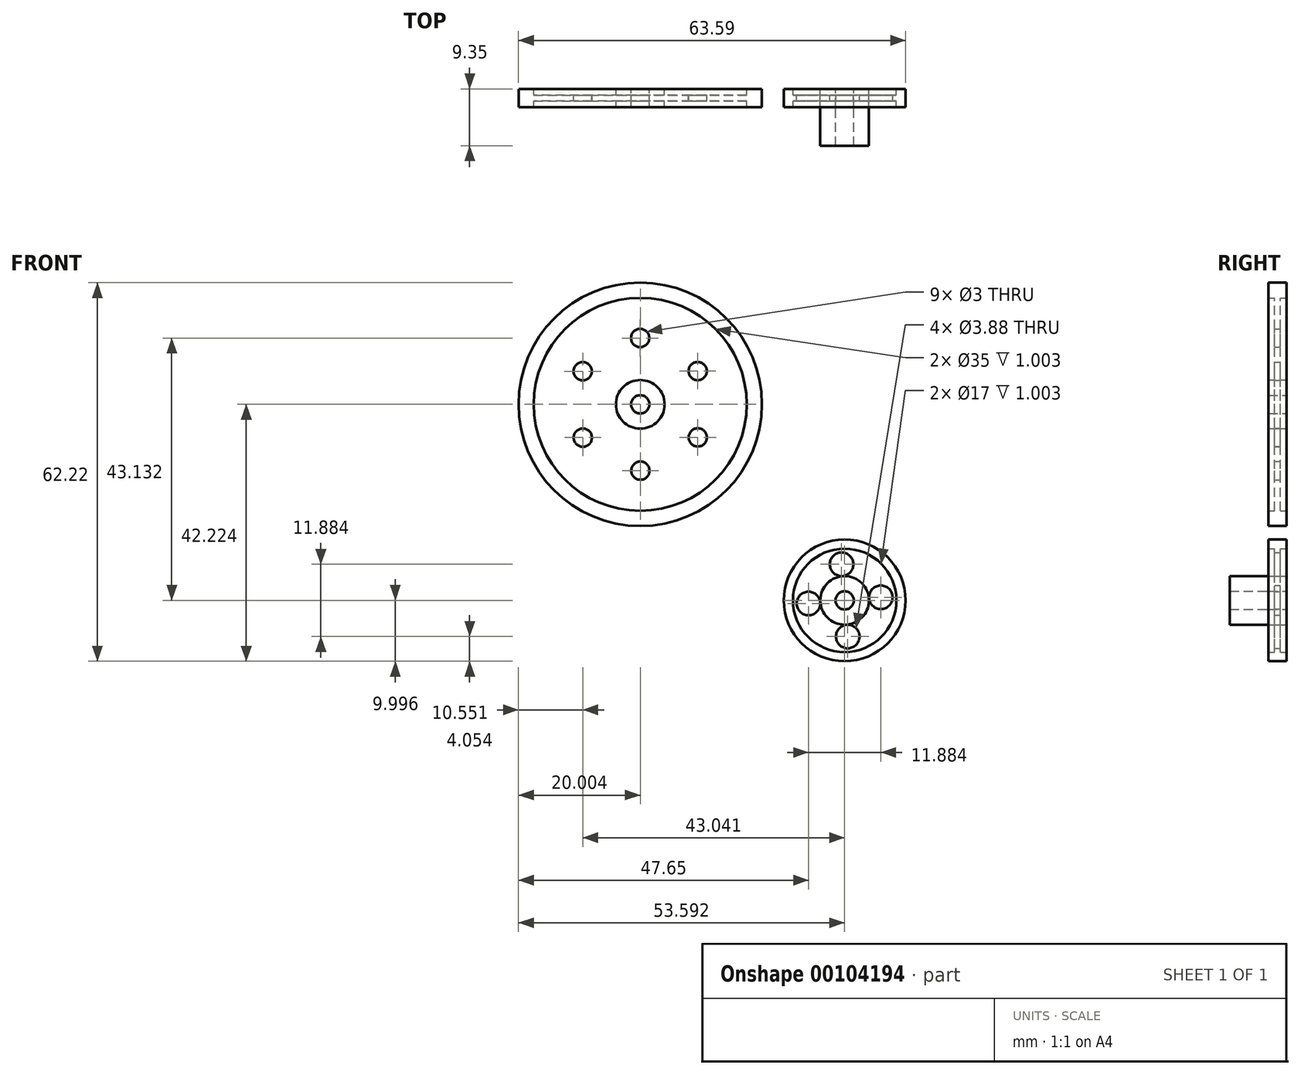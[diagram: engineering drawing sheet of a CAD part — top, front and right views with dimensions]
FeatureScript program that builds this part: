
annotation { "Feature Type Name" : "Feature", "Feature Type Description" : "" }
export const myFeature = defineFeature(function(context is Context, id is Id, definition is map)
    precondition{}
    {
        {
            var Q0;
            Q0=qCreatedBy(makeId("Front.planeOp"),FACE);
            var sketch = newSketch(context, id + "F0", { "sketchPlane" : qUnion([Q0])});
            skCircle(sketch, "E0", {"center": v(-85.9, 43.3) * mm, "radius": 20 * mm});
            skCircle(sketch, "E1", {"center": v(-85.9, 43.3) * mm, "radius": 4 * mm});
            skCircle(sketch, "E2", {"center": v(-85.9, 43.3) * mm, "radius": 1.5 * mm});
            skCircle(sketch, "E3", {"center": v(-85.9, 43.3) * mm, "radius": 17.5 * mm});
            skCircle(sketch, "E4.1.0", {"center": v(-85.88, 32.39) * mm, "radius": 1.5 * mm});
            skPoint(sketch, "E5.trimOffspring.end.orphan", {"position": v(-85.9, 47.8) * mm});
            skCircle(sketch, "E6.1.0", {"center": v(-76.44, 37.86) * mm, "radius": 1.5 * mm});
            skCircle(sketch, "E6.2.0", {"center": v(-76.46, 48.76) * mm, "radius": 1.5 * mm});
            skCircle(sketch, "E6.3.0", {"center": v(-85.92, 54.2) * mm, "radius": 1.5 * mm});
            skCircle(sketch, "E6.4.0", {"center": v(-95.35, 48.73) * mm, "radius": 1.5 * mm});
            skCircle(sketch, "E6.5.0", {"center": v(-95.33, 37.82) * mm, "radius": 1.5 * mm});
            skCircle(sketch, "E7", {"center": v(-52.3, 11.07) * mm, "radius": 10 * mm});
            skCircle(sketch, "E8", {"center": v(-52.3, 11.07) * mm, "radius": 8.5 * mm});
            skCircle(sketch, "E9", {"center": v(-52.3, 11.07) * mm, "radius": 4 * mm});
            skCircle(sketch, "E10", {"center": v(-52.3, 11.07) * mm, "radius": 1.5 * mm});
            skCircle(sketch, "E11.1.0", {"center": v(-52.81, 17) * mm, "radius": 1.94 * mm});
            skCircle(sketch, "E12.1.0", {"center": v(-58.25, 10.56) * mm, "radius": 1.94 * mm});
            skCircle(sketch, "E12.2.0", {"center": v(-51.8, 5.12) * mm, "radius": 1.94 * mm});
            skCircle(sketch, "E12.3.0", {"center": v(-46.37, 11.57) * mm, "radius": 1.94 * mm});
            skLineSegment(sketch, "E13.trimOffspring", {"start": v(-52.62, 15.05) * mm, "end": v(-52.92, 18.94) * mm});
            skSolve(sketch);
        }
        {
            var Q0;
            Q0 = qSketchRegion(id + "F0", true);
            var Q1;
            Q1=makeQuery(id+"F0.imprint","IMPRINT",FACE,{"disambiguationData":[TD([[makeQuery(id+"F0.imprint","IMPRINT",EDGE,{"derivedFrom":sQuery(id+"F0.wireOp",EDGE,"E1")}),1.0]])]});
            var Q2;
            Q2=makeQuery(id+"F0.imprint","IMPRINT",FACE,{"disambiguationData":[TD([[makeQuery(id+"F0.imprint","IMPRINT",EDGE,{"derivedFrom":sQuery(id+"F0.wireOp",EDGE,"E9")}),1.0]])]});
            extrude(context, id + "F1", {"entities" : qUnion([Q0, Q1, Q2]), "endBound" : BoundingType.SYMMETRIC, "depth" : 3 * mm});
        }
        {
            var Q0;
            Q0=makeQuery(id+"F0.imprint","IMPRINT",FACE,{"disambiguationData":[TD([[makeQuery(id+"F0.imprint","IMPRINT",EDGE,{"derivedFrom":sQuery(id+"F0.wireOp",EDGE,"E1")}),-1.0]])]});
            var Q1;
            Q1=makeQuery(id+"F0.imprint","IMPRINT",FACE,{"disambiguationData":[TD([[makeQuery(id+"F0.imprint","IMPRINT",EDGE,{"derivedFrom":sQuery(id+"F0.wireOp",EDGE,"E8")}),1.0]])]});
            extrude(context, id + "F2", {"entities" : qUnion([Q0, Q1]), "operationType" : NewBodyOperationType.ADD, "endBound" : BoundingType.SYMMETRIC, "depth" : 1 * mm});
        }
        {
            var Q0;
            Q0=makeQuery(id+"F1.opExtrude","CAP_FACE",FACE,{"disambiguationData":[OSD([sQuery(id+"F0.wireOp",EDGE,"E9"),sQuery(id+"F0.wireOp",EDGE,"E10")])],"isStart":false});
            extrude(context, id + "F3", {"entities" : qUnion([Q0]), "depth" : 6.35 * mm});
        }
    });
